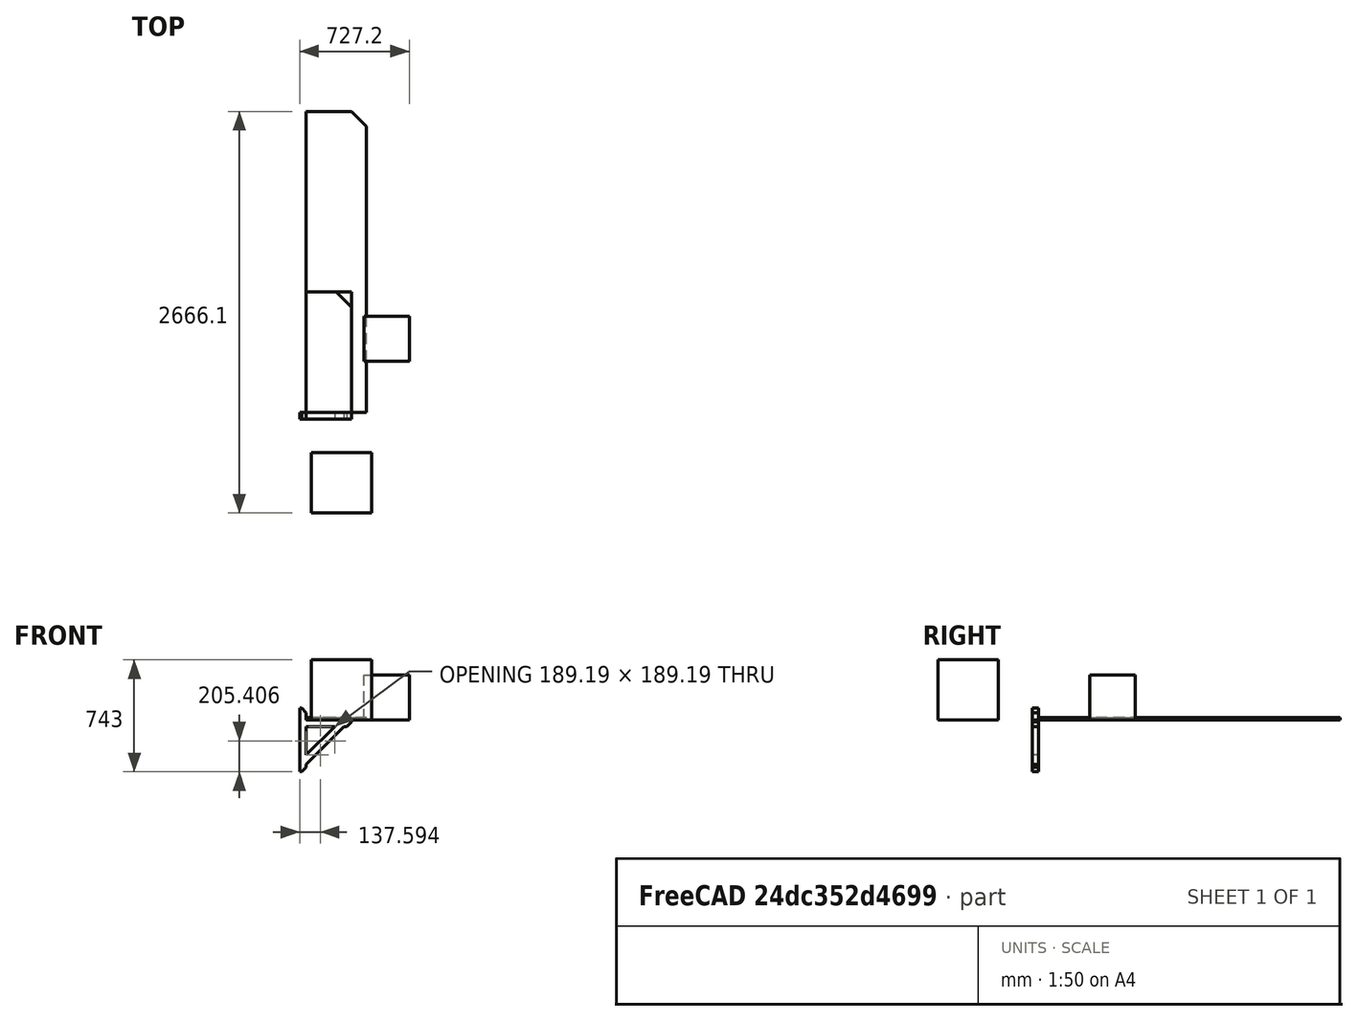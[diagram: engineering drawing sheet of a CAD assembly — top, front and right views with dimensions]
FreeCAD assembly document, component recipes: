
FREECAD ASSEMBLY — COMPONENT RECIPES ("shed_shelves")

This assembly document has 8 components, labeled P0..P7 below (a component is one placed body or linked part). 7 of them carry a construction recipe — the FreeCAD feature program that regenerates the part from scratch, quoted from this document or its linked companion documents; the rest are supplied as boundary geometry only. No exploded tour is included for this assembly.
COMPONENT P0 — geometry summary ("Part003"; no construction recipe available for this part):
  bounding box: 1306.1 x 649.2 x 400.0 mm
  tessellated surface: 24 triangles
  volume: 91000000 mm^3 (27% of its bounding box)
COMPONENT P1 — recipe-attached ("Part_2000x400x019", modeled in this document).
Construction recipe (the document's own serialized feature program — sketch geometry with constraints, then the solid features built on it; lengths are millimeters unless a unit is written):

FEATURE [Sketcher::SketchObject] Sketch
  ArcFitTolerance = 1e-06
  AttachmentSupport = -> [XY_Plane]
  FullyConstrained = true
  MakeInternals = false
  MapMode = 5
  sketch-geometry (4):
    g0: LineSegment StartX=0 StartY=0 StartZ=0 EndX=400 EndY=0 EndZ=0
    g1: LineSegment StartX=400 StartY=0 StartZ=0 EndX=400 EndY=2000 EndZ=0
    g2: LineSegment StartX=400 StartY=2000 StartZ=0 EndX=0 EndY=2000 EndZ=0
    g3: LineSegment StartX=0 StartY=2000 StartZ=0 EndX=0 EndY=0 EndZ=0
  constraints (11):
    c: Coincident(g0,g1)
    c: Coincident(g1,g2)
    c: Coincident(g2,g3)
    c: Coincident(g3,g0)
    c: Horizontal(g0)
    c: Horizontal(g2)
    c: Vertical(g1)
    c: Vertical(g3)
    c: Distance(g1,g3) = 400
    c: Distance(g0,g2) = 2000
    c: Coincident(g0,g-1)
FEATURE [PartDesign::Pad] Pad
  Direction = (0,0,1)
  Length = 18
  Length2 = 10
  Profile = -> Sketch
  ReferenceAxis = -> Sketch [N_Axis]
  Refine = true
  Suppressed = false
  Type = 0
FEATURE [PartDesign::Chamfer] Chamfer
  Angle = 45
  Base = -> Pad [Edge5]
  BaseFeature = -> Pad
  ChamferType = 0
  FlipDirection = false
  Refine = true
  Size = 100
  Size2 = 1
  SupportTransform = false
  Suppressed = false
  UseAllEdges = false
FEATURE [PartDesign::Body] Body
  AllowCompound = false
  Group = -> [Sketch,Pad,Chamfer]
  Origin = -> Origin
  Tip = -> Chamfer
COMPONENT P2 — recipe-attached ("Part_800x30x019", modeled in this document).
Construction recipe (the document's own serialized feature program — sketch geometry with constraints, then the solid features built on it; lengths are millimeters unless a unit is written):

FEATURE [Sketcher::SketchObject] Sketch002
  ArcFitTolerance = 1e-06
  AttachmentSupport = -> [XY_Plane004]
  FullyConstrained = true
  MakeInternals = false
  MapMode = 5
  sketch-geometry (4):
    g0: LineSegment StartX=0 StartY=0 StartZ=0 EndX=300 EndY=0 EndZ=0
    g1: LineSegment StartX=300 StartY=0 StartZ=0 EndX=300 EndY=800 EndZ=0
    g2: LineSegment StartX=300 StartY=800 StartZ=0 EndX=0 EndY=800 EndZ=0
    g3: LineSegment StartX=0 StartY=800 StartZ=0 EndX=0 EndY=0 EndZ=0
  constraints (11):
    c: Coincident(g0,g1)
    c: Coincident(g1,g2)
    c: Coincident(g2,g3)
    c: Coincident(g3,g0)
    c: Horizontal(g0)
    c: Horizontal(g2)
    c: Vertical(g1)
    c: Vertical(g3)
    c: Distance(g1,g3) = 300
    c: Distance(g0,g2) = 800
    c: Coincident(g0,g-1)
FEATURE [PartDesign::Pad] Pad002
  Direction = (0,0,1)
  Length = 18
  Length2 = 10
  Profile = -> Sketch002
  ReferenceAxis = -> Sketch002 [N_Axis]
  Refine = true
  Suppressed = false
  Type = 0
FEATURE [PartDesign::Chamfer] Chamfer001
  Angle = 45
  Base = -> Pad002 [Edge5]
  BaseFeature = -> Pad002
  ChamferType = 0
  FlipDirection = false
  Refine = true
  Size = 100
  Size2 = 1
  SupportTransform = false
  Suppressed = false
  UseAllEdges = false
FEATURE [PartDesign::Body] Body002
  AllowCompound = false
  Group = -> [Sketch002,Pad002,Chamfer001]
  Origin = -> Origin004
  Tip = -> Chamfer001
COMPONENT P3 — recipe-attached ("Part_800x400x019", modeled in this document).
Construction recipe (the document's own serialized feature program — sketch geometry with constraints, then the solid features built on it; lengths are millimeters unless a unit is written):

FEATURE [Sketcher::SketchObject] Sketch001
  ArcFitTolerance = 1e-06
  AttachmentSupport = -> [XY_Plane002]
  FullyConstrained = true
  MakeInternals = false
  MapMode = 5
  sketch-geometry (4):
    g0: LineSegment StartX=0 StartY=0 StartZ=0 EndX=300 EndY=0 EndZ=0
    g1: LineSegment StartX=300 StartY=0 StartZ=0 EndX=300 EndY=800 EndZ=0
    g2: LineSegment StartX=300 StartY=800 StartZ=0 EndX=0 EndY=800 EndZ=0
    g3: LineSegment StartX=0 StartY=800 StartZ=0 EndX=0 EndY=0 EndZ=0
  constraints (11):
    c: Coincident(g0,g1)
    c: Coincident(g1,g2)
    c: Coincident(g2,g3)
    c: Coincident(g3,g0)
    c: Horizontal(g0)
    c: Horizontal(g2)
    c: Vertical(g1)
    c: Vertical(g3)
    c: Distance(g1,g3) = 300
    c: Distance(g0,g2) = 800
    c: Coincident(g0,g-1)
FEATURE [PartDesign::Pad] Pad001
  Direction = (0,0,1)
  Length = 18
  Length2 = 10
  Profile = -> Sketch001
  ReferenceAxis = -> Sketch001 [N_Axis]
  Refine = true
  Suppressed = false
  Type = 0
FEATURE [PartDesign::Body] Body001
  AllowCompound = false
  Group = -> [Sketch001,Pad001]
  Origin = -> Origin002
  Tip = -> Pad001
COMPONENT P4 — recipe-attached ("shelf_boy001", modeled in this document).
Construction recipe (the document's own serialized feature program — sketch geometry with constraints, then the solid features built on it; lengths are millimeters unless a unit is written):

FEATURE [Sketcher::SketchObject] Sketch003
  ArcFitTolerance = 1e-06
  AttachmentSupport = -> [XZ_Plane009]
  FullyConstrained = true
  MakeInternals = false
  MapMode = 5
  Placement = pos=(0,0,0) rot=(1,0,0;1.5708rad)
  expr: Constraints[52] = .Constraints.edgeradii
  expr: Constraints[53] = .Constraints.edgeradii
  expr: Constraints[54] = .Constraints.wood_thinckness
  expr: Constraints[66] = .Constraints.wood_thinckness
  sketch-geometry (32):
    g0: LineSegment StartX=-43 StartY=80 StartZ=0 EndX=-43 EndY=-343 EndZ=0
    g1: LineSegment StartX=-43 StartY=-343 StartZ=0 EndX=-30 EndY=-343 EndZ=0
    g2: LineSegment StartX=0 StartY=-313 StartZ=0 EndX=0 EndY=50 EndZ=0
    g3: LineSegment StartX=-30 StartY=80 StartZ=0 EndX=-43 EndY=80 EndZ=0
    g4: LineSegment StartX=0 StartY=0 StartZ=0 EndX=0 EndY=-43 EndZ=0
    g5: LineSegment StartX=0 StartY=-43 StartZ=0 EndX=270 EndY=-43 EndZ=0
    g6: LineSegment StartX=300 StartY=-13 StartZ=0 EndX=300 EndY=0 EndZ=0
    g7: LineSegment StartX=300 StartY=0 StartZ=0 EndX=0 EndY=0 EndZ=0
    g8: LineSegment [constr] StartX=0 StartY=0 StartZ=0 EndX=400 EndY=0 EndZ=0
    g9: LineSegment [constr] StartX=400 StartY=0 StartZ=0 EndX=400 EndY=18 EndZ=0
    g10: LineSegment [constr] StartX=400 StartY=18 StartZ=0 EndX=0 EndY=18 EndZ=0
    g11: LineSegment [constr] StartX=0 StartY=18 StartZ=0 EndX=0 EndY=0 EndZ=0
    g12: LineSegment [constr] StartX=-43 StartY=-343 StartZ=0 EndX=300 EndY=0 EndZ=0
    g13: ArcOfCircle [constr] CenterX=-30 CenterY=50 CenterZ=0 NormalX=0 NormalY=0 NormalZ=1 AngleXU=0 Radius=30 StartAngle=0 EndAngle=1.5708
    g14: GeomPoint [constr] X=0 Y=80 Z=0
    g15: LineSegment StartX=0 StartY=50 StartZ=0 EndX=-30 EndY=80 EndZ=0
    g16: ArcOfCircle [constr] CenterX=270 CenterY=-13 CenterZ=0 NormalX=0 NormalY=0 NormalZ=1 AngleXU=0 Radius=30 StartAngle=4.71239 EndAngle=6.28319
    g17: GeomPoint [constr] X=300 Y=-43 Z=0
    g18: LineSegment StartX=270 StartY=-43 StartZ=0 EndX=300 EndY=-13 EndZ=0
    g19: ArcOfCircle [constr] CenterX=-30 CenterY=-313 CenterZ=0 NormalX=0 NormalY=0 NormalZ=1 AngleXU=0 Radius=30 StartAngle=4.71239 EndAngle=6.28319
    g20: GeomPoint [constr] X=0 Y=-343 Z=0
    g21: LineSegment StartX=-30 StartY=-343 StartZ=0 EndX=0 EndY=-313 EndZ=0
    g22: LineSegment StartX=3.6e-15 StartY=-293 StartZ=0 EndX=250 EndY=-43 EndZ=0
    g23: LineSegment [constr] StartX=-30.4056 StartY=-262.594 StartZ=0 EndX=219.594 EndY=-12.5944 EndZ=0
    g24: LineSegment [constr] StartX=-30.4056 StartY=-262.594 StartZ=0 EndX=3.6e-15 EndY=-293 EndZ=0
    g25: LineSegment [constr] StartX=219.594 StartY=-12.5944 StartZ=0 EndX=250 EndY=-43 EndZ=0
    g26: LineSegment StartX=3.6e-15 StartY=-293 StartZ=0 EndX=3.6e-15 EndY=-232.189 EndZ=0
    g27: LineSegment StartX=3.6e-15 StartY=-232.189 StartZ=0 EndX=189.189 EndY=-43 EndZ=0
    g28: LineSegment StartX=189.189 StartY=-43 StartZ=0 EndX=250 EndY=-43 EndZ=0
    g29: LineSegment [constr] StartX=-30 StartY=-343 StartZ=0 EndX=-43 EndY=-356 EndZ=0
    g30: LineSegment [constr] StartX=-30 StartY=80 StartZ=0 EndX=-43 EndY=93 EndZ=0
    g31: LineSegment [constr] StartX=-43 StartY=93 StartZ=0 EndX=-43 EndY=-356 EndZ=0
  constraints (88):
    c: Coincident(g3,g0)
    c: Vertical(g0)
    c: Vertical(g2)
    c: Horizontal(g1)
    c: Horizontal(g3)
    c: Coincident(g4,g5)
    c: Coincident(g6,g7)
    c: Coincident(g7,g4)
    c: Vertical(g4)
    c: Vertical(g6)
    c: Horizontal(g5)
    c: Horizontal(g7)
    c: PointOnObject(g4,g2)
    c: Distance(g17,g6) = 43  'wood_thinckness'
    c: Distance(g14,g4) = 80
    c: Coincident(g8,g9)
    c: Coincident(g9,g10)
    c: Coincident(g10,g11)
    c: Coincident(g11,g8)
    c: Horizontal(g8)
    c: Horizontal(g10)
    c: Vertical(g9)
    c: Vertical(g11)
    c: Coincident(g8,g-1)
    c: DistanceX(g10,g10) = 400
    c: Distance(g9,g9) = 18
    c: Coincident(g1,g0)
    c: Coincident(g4,g8)
    c: Coincident(g12,g0)
    c: Coincident(g12,g6)
    c: Angle(g10,g12) = 0.785398
    c: DistanceY(g0,g0) = 423
    c: Distance(g8,g6) = 100
    c: PointOnObject(g14,g2)
    c: PointOnObject(g14,g3)
    c: Tangent(g2,g13) = -1.5708
    c: Tangent(g3,g13) = -1.5708
    c: Coincident(g15,g2)
    c: Coincident(g15,g3)
    c: PointOnObject(g17,g5)
    c: PointOnObject(g17,g6)
    c: Tangent(g5,g16) = -1.5708
    c: Tangent(g6,g16) = -1.5708
    c: Coincident(g18,g5)
    c: Coincident(g18,g6)
    c: PointOnObject(g20,g1)
    c: PointOnObject(g20,g2)
    c: Tangent(g1,g19) = -1.5708
    c: Tangent(g2,g19) = -1.5708
    c: Coincident(g21,g1)
    c: Coincident(g21,g2)
    c: Radius(g16) = 30  'edgeradii'
    c: Radius(g19) = 30
    c: Radius(g13) = 30
    c: Distance(g0,g2) = 43
    c: DistanceX(g7,g7) = 300
    c: PointOnObject(g22,g2)
    c: PointOnObject(g22,g5)
    c: Parallel(g23,g22)
    c: Coincident(g24,g23)
    c: Coincident(g24,g22)
    c: Coincident(g25,g22)
    c: Coincident(g23,g25)
    c: Parallel(g24,g25)
    c: Perpendicular(g25,g23,g23) = 1.5708
    c: Parallel(g22,g12)
    c: Distance(g25,g25) = 43
    c: Coincident(g22,g26)
    c: PointOnObject(g26,g23)
    c: Vertical(g26)
    c: Coincident(g26,g27)
    c: Coincident(g28,g22)
    c: Coincident(g28,g27)
    c: PointOnObject(g27,g23)
    c: PointOnObject(g27,g5)
    c: Distance(g22,g22) = 353.553
    c: Distance(g2,g4) = 50
    c: Distance(g2,g22) = 20
    c: Coincident(g29,g1)
    c: Coincident(g30,g3)
    c: Parallel(g15,g30)
    c: Parallel(g29,g21)
    c: Coincident(g31,g30)
    c: Coincident(g31,g29)
    c: Vertical(g31)
    c: Vertical(g29,g0)
    c: DistanceY(g29,g30) = 449
    c: DistanceY(g29,g22) = 63
FEATURE [PartDesign::Pad] Pad003
  Direction = (0,-1,2e-16)
  Length = 43
  Length2 = 10
  Placement = pos=(0,0,0) rot=(1,0,0;1.5708rad)
  Profile = -> Sketch003
  ReferenceAxis = -> Sketch003 [N_Axis]
  Refine = true
  Suppressed = false
  Type = 0
FEATURE [PartDesign::Body] Body003
  AllowCompound = false
  Group = -> [Sketch003,Pad003]
  Origin = -> Origin009
  Tip = -> Pad003
COMPONENT P5 — same part as P4; its construction recipe is shown at P4.
COMPONENT P6 — same part as P4; its construction recipe is shown at P4.
COMPONENT P7 — same part as P4; its construction recipe is shown at P4.
PROVENANCE & LICENSES
A FreeCAD (.FCStd) document from a public repository crawl; recipes are the document's own serialized feature recipes (and, for linked parts, companion documents' recipes).
License: as declared in the source repository (recorded in the dataset sidecar).
